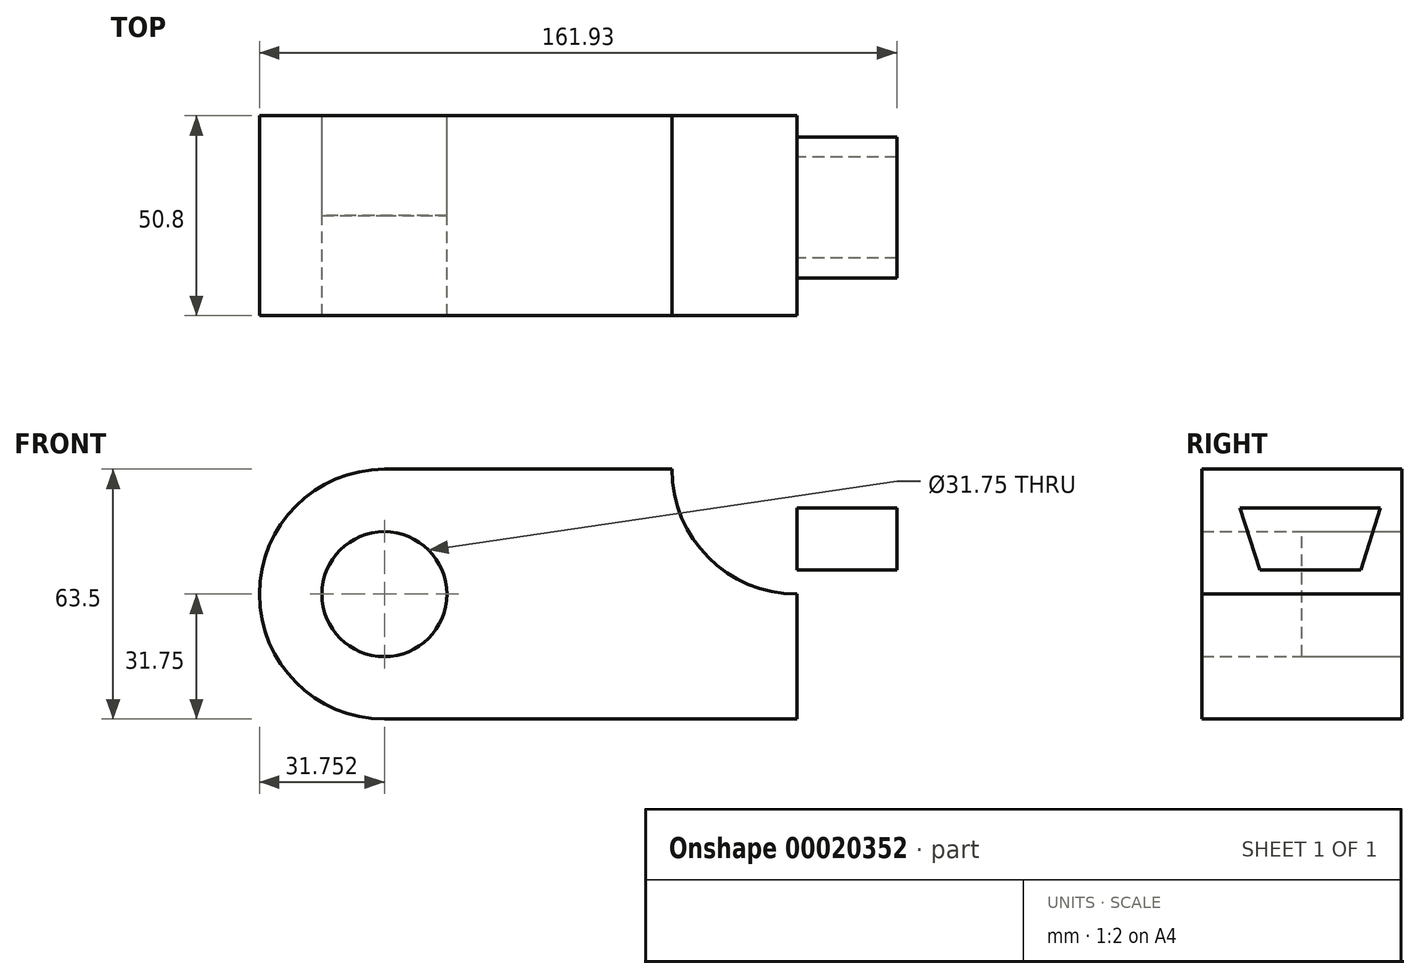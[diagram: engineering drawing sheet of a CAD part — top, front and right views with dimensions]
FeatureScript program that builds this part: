
annotation { "Feature Type Name" : "Feature", "Feature Type Description" : "" }
export const myFeature = defineFeature(function(context is Context, id is Id, definition is map)
    precondition{}
    {
        {
            var Q0;
            Q0=qCreatedBy(makeId("Front.planeOp"),FACE);
            var sketch = newSketch(context, id + "F0", { "sketchPlane" : qUnion([Q0])});
            skLineSegment(sketch, "E0.bottom", {"start": v(-33.83, 31.75) * mm, "end": v(39.2, 31.75) * mm});
            skLineSegment(sketch, "E0.top", {"start": v(-33.83, -31.75) * mm, "end": v(70.95, -31.75) * mm});
            skLineSegment(sketch, "E0.right", {"start": v(70.95, 0) * mm, "end": v(70.95, -31.75) * mm});
            skArc(sketch, "E1", {"start": v(-33.83, 31.75) * mm, "mid": v(-65.58, 0) * mm, "end": v(-33.83, -31.75) * mm});
            skCircle(sketch, "E2", {"center": v(-33.83, 0) * mm, "radius": 15.88 * mm});
            skArc(sketch, "E3", {"start": v(39.2, 31.75) * mm, "mid": v(48.5, 9.3) * mm, "end": v(70.95, 0) * mm});
            skSolve(sketch);
        }
        {
            var Q0;
            Q0=makeQuery(id+"F0.imprint","IMPRINT",FACE,{"disambiguationData":[TD([[makeQuery(id+"F0.imprint","IMPRINT",EDGE,{"derivedFrom":sQuery(id+"F0.wireOp",EDGE,"E0.bottom")}),-1.0]])]});
            extrude(context, id + "F1", {"entities" : qUnion([Q0]), "depth" : 50.8 * mm});
        }
        {
            var Q0;
            Q0=makeQuery(id+"F0.imprint","IMPRINT",FACE,{"disambiguationData":[TD([[makeQuery(id+"F0.imprint","IMPRINT",EDGE,{"derivedFrom":sQuery(id+"F0.wireOp",EDGE,"E2")}),1.0]])]});
            extrude(context, id + "F2", {"entities" : qUnion([Q0]), "depth" : 25.4 * mm});
        }
        {
            var Q0;
            Q0=makeQuery(id+"F1.opExtrude","SWEPT_FACE",FACE,{"disambiguationData":[OSD([sQuery(id+"F0.wireOp",EDGE,"E0.right")])]});
            var sketch = newSketch(context, id + "F3", { "sketchPlane" : qUnion([Q0])});
            skLineSegment(sketch, "E4", {"start": v(-41.2, 21.9) * mm, "end": v(-36.13, 6.1) * mm});
            skLineSegment(sketch, "E5", {"start": v(-36.13, 6.1) * mm, "end": v(-10.5, 6.1) * mm});
            skLineSegment(sketch, "E6", {"start": v(-10.5, 6.1) * mm, "end": v(-5.43, 21.9) * mm});
            skLineSegment(sketch, "E7", {"start": v(-5.43, 21.9) * mm, "end": v(-41.2, 21.9) * mm});
            skSolve(sketch);
        }
        {
            var Q0;
            Q0=makeQuery(id+"F3.imprint","IMPRINT",FACE,{"disambiguationData":[TD([[makeQuery(id+"F3.imprint","IMPRINT",EDGE,{"derivedFrom":sQuery(id+"F3.wireOp",EDGE,"E4")}),1.0]])]});
            extrude(context, id + "F4", {"entities" : qUnion([Q0]), "depth" : 25.4 * mm});
        }
    });
